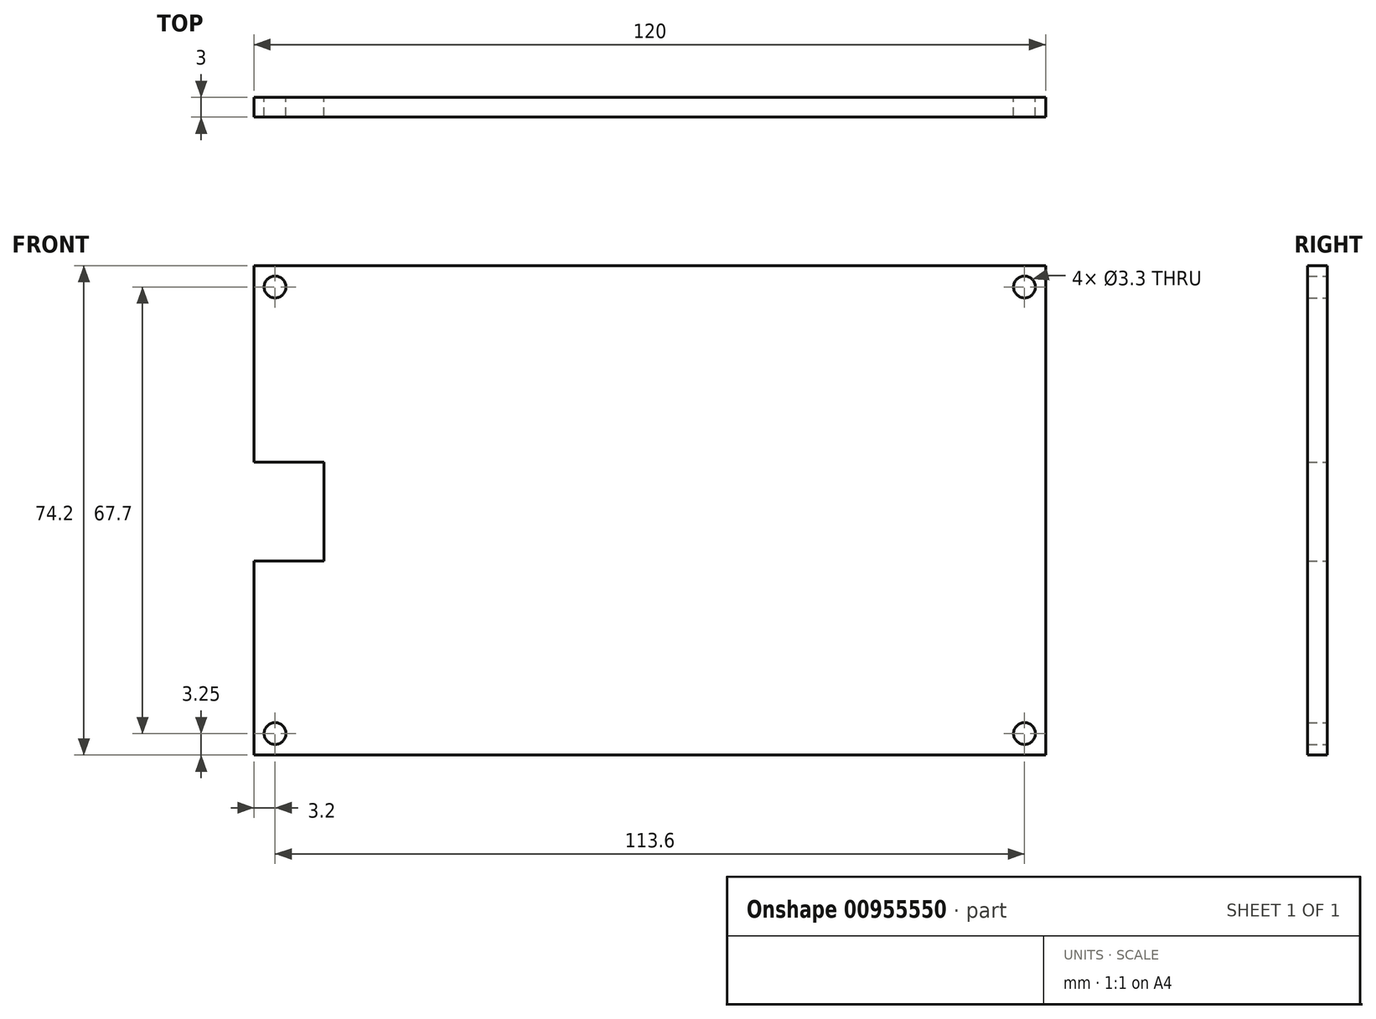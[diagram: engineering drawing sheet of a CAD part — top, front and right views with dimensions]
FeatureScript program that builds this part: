
annotation { "Feature Type Name" : "Feature", "Feature Type Description" : "" }
export const myFeature = defineFeature(function(context is Context, id is Id, definition is map)
    precondition{}
    {
        {
            var Q0;
            Q0=qCreatedBy(makeId("Front.planeOp"),FACE);
            var sketch = newSketch(context, id + "F0", { "sketchPlane" : qUnion([Q0])});
            skLineSegment(sketch, "E0.bottom", {"start": v(60, -37.1) * mm, "end": v(-60, -37.1) * mm});
            skLineSegment(sketch, "E0.top", {"start": v(60, 37.1) * mm, "end": v(-60, 37.1) * mm});
            skLineSegment(sketch, "E0.left", {"start": v(60, -37.1) * mm, "end": v(60, 37.1) * mm});
            skLineSegment(sketch, "E0.right", {"start": v(-60, -37.1) * mm, "end": v(-60, -7.68) * mm});
            skPoint(sketch, "E0.middle", {"position": v(0, 0) * mm});
            skLineSegment(sketch, "E1.bottom", {"start": v(56.8, -33.85) * mm, "end": v(-56.8, -33.85) * mm, "construction": true});
            skLineSegment(sketch, "E1.top", {"start": v(56.8, 33.85) * mm, "end": v(-56.8, 33.85) * mm, "construction": true});
            skLineSegment(sketch, "E1.left", {"start": v(56.8, -33.85) * mm, "end": v(56.8, 33.85) * mm, "construction": true});
            skLineSegment(sketch, "E1.right", {"start": v(-56.8, -33.85) * mm, "end": v(-56.8, 33.85) * mm, "construction": true});
            skCircle(sketch, "E2", {"center": v(-56.8, 33.85) * mm, "radius": 1.65 * mm});
            skCircle(sketch, "E3", {"center": v(-56.8, -33.85) * mm, "radius": 1.65 * mm});
            skCircle(sketch, "E4", {"center": v(56.8, -33.85) * mm, "radius": 1.65 * mm});
            skCircle(sketch, "E5", {"center": v(56.8, 33.85) * mm, "radius": 1.65 * mm});
            skLineSegment(sketch, "E6.bottom", {"start": v(-60, 7.32) * mm, "end": v(-49.38, 7.32) * mm});
            skLineSegment(sketch, "E6.top", {"start": v(-60, -7.68) * mm, "end": v(-49.38, -7.68) * mm});
            skLineSegment(sketch, "E6.right", {"start": v(-49.38, 7.32) * mm, "end": v(-49.38, -7.68) * mm});
            skLineSegment(sketch, "E7.trimOffspring", {"start": v(-60, 7.32) * mm, "end": v(-60, 37.1) * mm});
            skSolve(sketch);
        }
        {
            var Q0;
            Q0 = qSketchRegion(id + "F0", true);
            extrude(context, id + "F1", {"entities" : qUnion([Q0]), "depth" : 3 * mm, "offsetDistance" : 25 * mm});
        }
    });
